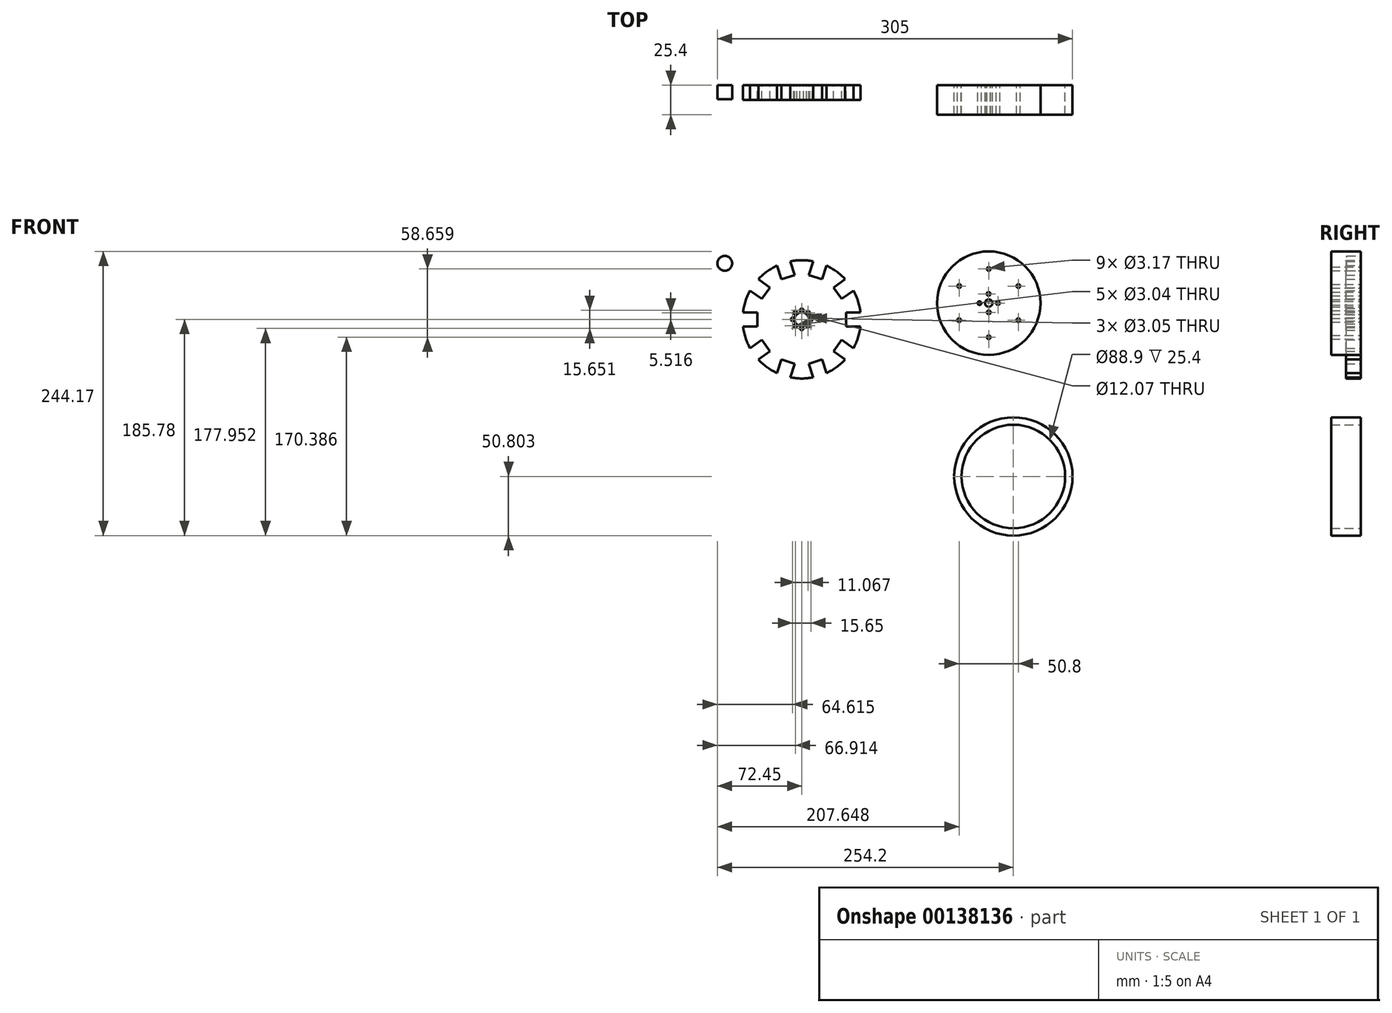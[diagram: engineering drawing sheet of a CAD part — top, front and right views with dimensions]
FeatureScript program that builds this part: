
annotation { "Feature Type Name" : "Feature", "Feature Type Description" : "" }
export const myFeature = defineFeature(function(context is Context, id is Id, definition is map)
    precondition{}
    {
        {
            var Q0;
            Q0=qCreatedBy(makeId("Front.planeOp"),FACE);
            var sketch = newSketch(context, id + "F0", { "sketchPlane" : qUnion([Q0])});
            skLineSegment(sketch, "E0.0", {"start": v(-6.03, 38.1) * mm, "end": v(6.03, 38.1) * mm});
            skLineSegment(sketch, "E0.2", {"start": v(17.51, 34.37) * mm, "end": v(27.28, 27.28) * mm});
            skLineSegment(sketch, "E0.4", {"start": v(34.37, 17.51) * mm, "end": v(38.1, 6.03) * mm});
            skLineSegment(sketch, "E0.6", {"start": v(38.1, -6.03) * mm, "end": v(34.37, -17.51) * mm});
            skLineSegment(sketch, "E0.8", {"start": v(27.28, -27.28) * mm, "end": v(17.51, -34.37) * mm});
            skLineSegment(sketch, "E0.10", {"start": v(6.03, -38.1) * mm, "end": v(-6.03, -38.1) * mm});
            skLineSegment(sketch, "E0.12", {"start": v(-17.51, -34.37) * mm, "end": v(-27.28, -27.28) * mm});
            skLineSegment(sketch, "E0.14", {"start": v(-34.37, -17.51) * mm, "end": v(-38.1, -6.03) * mm});
            skLineSegment(sketch, "E0.16", {"start": v(-38.1, 6.03) * mm, "end": v(-34.37, 17.51) * mm});
            skLineSegment(sketch, "E0.18", {"start": v(-27.28, 27.28) * mm, "end": v(-17.51, 34.37) * mm});
            skPoint(sketch, "E0.0.midPoint", {"position": v(0, 38.1) * mm});
            skLineSegment(sketch, "E1", {"start": v(6.03, 38.1) * mm, "end": v(9.85, 49.84) * mm});
            skLineSegment(sketch, "E2", {"start": v(-34.37, 17.51) * mm, "end": v(-44.35, 24.77) * mm});
            skLineSegment(sketch, "E3", {"start": v(-38.1, 6.03) * mm, "end": v(-50.44, 6.03) * mm});
            skLineSegment(sketch, "E4", {"start": v(-38.1, -6.03) * mm, "end": v(-50.44, -6.03) * mm});
            skLineSegment(sketch, "E5", {"start": v(-34.37, -17.51) * mm, "end": v(-44.35, -24.77) * mm});
            skLineSegment(sketch, "E6", {"start": v(-27.28, -27.28) * mm, "end": v(-37.26, -34.53) * mm});
            skLineSegment(sketch, "E7", {"start": v(-17.51, -34.37) * mm, "end": v(-21.33, -46.1) * mm});
            skLineSegment(sketch, "E8", {"start": v(-6.03, -38.1) * mm, "end": v(-9.85, -49.84) * mm});
            skLineSegment(sketch, "E9", {"start": v(6.03, -38.1) * mm, "end": v(9.85, -49.84) * mm});
            skLineSegment(sketch, "E10", {"start": v(17.51, -34.37) * mm, "end": v(21.33, -46.1) * mm});
            skLineSegment(sketch, "E11", {"start": v(27.28, -27.28) * mm, "end": v(37.26, -34.53) * mm});
            skLineSegment(sketch, "E12", {"start": v(34.37, -17.51) * mm, "end": v(44.35, -24.77) * mm});
            skLineSegment(sketch, "E13", {"start": v(38.1, -6.03) * mm, "end": v(50.44, -6.03) * mm});
            skLineSegment(sketch, "E14", {"start": v(38.1, 6.03) * mm, "end": v(50.44, 6.03) * mm});
            skLineSegment(sketch, "E15", {"start": v(34.37, 17.51) * mm, "end": v(44.35, 24.77) * mm});
            skLineSegment(sketch, "E16", {"start": v(27.28, 27.28) * mm, "end": v(37.26, 34.53) * mm});
            skLineSegment(sketch, "E17", {"start": v(17.51, 34.37) * mm, "end": v(21.33, 46.1) * mm});
            skArc(sketch, "E18", {"start": v(-21.33, 46.1) * mm, "mid": v(-29.86, 41.1) * mm, "end": v(-37.26, 34.53) * mm});
            skLineSegment(sketch, "E19", {"start": v(-27.28, 27.28) * mm, "end": v(-37.26, 34.53) * mm});
            skLineSegment(sketch, "E20", {"start": v(-17.51, 34.37) * mm, "end": v(-21.33, 46.1) * mm});
            skLineSegment(sketch, "E21", {"start": v(-9.85, 49.84) * mm, "end": v(-6.03, 38.1) * mm});
            skArc(sketch, "E22.trimOffspring", {"start": v(-44.35, 24.77) * mm, "mid": v(-48.31, 15.7) * mm, "end": v(-50.44, 6.03) * mm});
            skArc(sketch, "E23.trimOffspring", {"start": v(-50.44, -6.03) * mm, "mid": v(-48.31, -15.7) * mm, "end": v(-44.35, -24.77) * mm});
            skArc(sketch, "E24.trimOffspring", {"start": v(-9.85, -49.84) * mm, "mid": v(0, -50.8) * mm, "end": v(9.85, -49.84) * mm});
            skArc(sketch, "E25.trimOffspring", {"start": v(21.33, -46.1) * mm, "mid": v(29.86, -41.1) * mm, "end": v(37.26, -34.53) * mm});
            skArc(sketch, "E26.trimOffspring", {"start": v(-37.26, -34.53) * mm, "mid": v(-29.86, -41.1) * mm, "end": v(-21.33, -46.1) * mm});
            skArc(sketch, "E27.trimOffspring", {"start": v(9.85, 49.84) * mm, "mid": v(0, 50.8) * mm, "end": v(-9.85, 49.84) * mm});
            skArc(sketch, "E28.trimOffspring", {"start": v(37.26, 34.53) * mm, "mid": v(29.86, 41.1) * mm, "end": v(21.33, 46.1) * mm});
            skArc(sketch, "E29.trimOffspring", {"start": v(50.44, 6.03) * mm, "mid": v(48.31, 15.7) * mm, "end": v(44.35, 24.77) * mm});
            skArc(sketch, "E30.trimOffspring", {"start": v(44.35, -24.77) * mm, "mid": v(48.31, -15.7) * mm, "end": v(50.44, -6.03) * mm});
            skLineSegment(sketch, "E31", {"start": v(-38.1, -6.03) * mm, "end": v(-38.1, 6.03) * mm});
            skLineSegment(sketch, "E32", {"start": v(-34.37, 17.51) * mm, "end": v(-27.28, 27.28) * mm});
            skLineSegment(sketch, "E33", {"start": v(-17.51, 34.37) * mm, "end": v(-6.03, 38.1) * mm});
            skLineSegment(sketch, "E34", {"start": v(6.03, 38.1) * mm, "end": v(17.51, 34.37) * mm});
            skLineSegment(sketch, "E35", {"start": v(27.28, 27.28) * mm, "end": v(34.37, 17.51) * mm});
            skLineSegment(sketch, "E36", {"start": v(38.1, 6.03) * mm, "end": v(38.1, -6.03) * mm});
            skLineSegment(sketch, "E37", {"start": v(34.37, -17.51) * mm, "end": v(27.28, -27.28) * mm});
            skLineSegment(sketch, "E38", {"start": v(17.51, -34.37) * mm, "end": v(6.03, -38.1) * mm});
            skLineSegment(sketch, "E39", {"start": v(-6.03, -38.1) * mm, "end": v(-17.51, -34.37) * mm});
            skLineSegment(sketch, "E40", {"start": v(-27.28, -27.28) * mm, "end": v(-34.37, -17.51) * mm});
            skCircle(sketch, "E41", {"center": v(0, 0) * mm, "radius": 6.03 * mm});
            skCircle(sketch, "E42.cCircle", {"center": v(0, 0) * mm, "radius": 6.03 * mm, "construction": true});
            skPoint(sketch, "E42.0.midPoint", {"position": v(0, 6.03) * mm});
            skPoint(sketch, "E43.orphan", {"position": v(0, -6.03) * mm});
            skCircle(sketch, "E44", {"center": v(0, -7.83) * mm, "radius": 1.52 * mm});
            skPoint(sketch, "E45.orphan", {"position": v(0, -6.31) * mm});
            skPoint(sketch, "E46.start.orphan", {"position": v(0, -9.35) * mm});
            skPoint(sketch, "E47.orphan", {"position": v(4.27, -4.27) * mm});
            skPoint(sketch, "E48.orphan", {"position": v(2.5, -6.03) * mm});
            skCircle(sketch, "E49", {"center": v(5.53, -5.53) * mm, "radius": 1.52 * mm});
            skPoint(sketch, "E50.orphan", {"position": v(4.45, -4.45) * mm});
            skPoint(sketch, "E51.end.orphan", {"position": v(6.6, -6.6) * mm});
            skPoint(sketch, "E52.endSnap0", {"position": v(6.03, 0) * mm});
            skCircle(sketch, "E53", {"center": v(7.81, 0) * mm, "radius": 1.52 * mm});
            skPoint(sketch, "E54.orphan", {"position": v(9.34, 0) * mm});
            skPoint(sketch, "E52.start.orphan", {"position": v(6.3, 0) * mm});
            skPoint(sketch, "E42.2.end.orphan", {"position": v(6.03, -2.5) * mm});
            skPoint(sketch, "E55.orphan", {"position": v(4.27, 4.27) * mm});
            skCircle(sketch, "E56", {"center": v(5.53, 5.53) * mm, "radius": 1.52 * mm});
            skPoint(sketch, "E57.orphan", {"position": v(6.6, 6.6) * mm});
            skPoint(sketch, "E58.end.orphan", {"position": v(4.46, 4.46) * mm});
            skPoint(sketch, "E59.orphan", {"position": v(6.03, 2.5) * mm});
            skPoint(sketch, "E60.orphan", {"position": v(2.5, 6.03) * mm});
            skCircle(sketch, "E61", {"center": v(0, 7.82) * mm, "radius": 1.52 * mm});
            skPoint(sketch, "E62.orphan", {"position": v(0, 9.34) * mm});
            skPoint(sketch, "E63.start.orphan", {"position": v(0, 6.3) * mm});
            skPoint(sketch, "E64.orphan", {"position": v(-4.27, 4.27) * mm});
            skPoint(sketch, "E65.orphan", {"position": v(-2.5, 6.03) * mm});
            skCircle(sketch, "E66", {"center": v(-5.52, 5.52) * mm, "radius": 1.52 * mm});
            skPoint(sketch, "E67.orphan", {"position": v(-6.6, 6.6) * mm});
            skPoint(sketch, "E68.start.orphan", {"position": v(-4.44, 4.44) * mm});
            skPoint(sketch, "E69.endSnap0", {"position": v(-6.03, 0) * mm});
            skPoint(sketch, "E70.orphan", {"position": v(-6.03, 2.5) * mm});
            skCircle(sketch, "E71", {"center": v(-7.83, 0) * mm, "radius": 1.53 * mm});
            skPoint(sketch, "E72.orphan", {"position": v(-6.3, 0) * mm});
            skPoint(sketch, "E73.start.orphan", {"position": v(-9.36, 0) * mm});
            skPoint(sketch, "E74.orphan", {"position": v(-4.27, -4.27) * mm});
            skPoint(sketch, "E75.orphan", {"position": v(-2.5, -6.03) * mm});
            skPoint(sketch, "E42.5.end.orphan", {"position": v(-6.03, -2.5) * mm});
            skCircle(sketch, "E76", {"center": v(-5.54, -5.54) * mm, "radius": 1.52 * mm});
            skPoint(sketch, "E77.orphan", {"position": v(-4.46, -4.46) * mm});
            skPoint(sketch, "E78.end.orphan", {"position": v(-6.6, -6.6) * mm});
            skSolve(sketch);
        }
        {
            var Q0;
            Q0 = qSketchRegion(id + "F0", true);
            extrude(context, id + "F1", {"entities" : qUnion([Q0]), "depth" : 12.7 * mm});
        }
        {
            var Q0;
            Q0=qCreatedBy(makeId("Front.planeOp"),FACE);
            var sketch = newSketch(context, id + "F2", { "sketchPlane" : qUnion([Q0])});
            skCircle(sketch, "E79", {"center": v(-66.1, 48.1) * mm, "radius": 6.35 * mm});
            skSolve(sketch);
        }
        {
            var Q0;
            Q0 = qSketchRegion(id + "F2", true);
            extrude(context, id + "F3", {"entities" : qUnion([Q0]), "depth" : 12.06 * mm});
        }
        {
            var Q0;
            Q0=qCreatedBy(makeId("Front.planeOp"),FACE);
            var sketch = newSketch(context, id + "F4", { "sketchPlane" : qUnion([Q0])});
            skCircle(sketch, "E80", {"center": v(160.6, 13.94) * mm, "radius": 44.45 * mm});
            skCircle(sketch, "E81", {"center": v(160.6, 13.94) * mm, "radius": 3.18 * mm});
            skPoint(sketch, "E82.0.midPoint", {"position": v(186, 13.94) * mm});
            skCircle(sketch, "E83", {"center": v(135.2, 28.6) * mm, "radius": 1.59 * mm});
            skCircle(sketch, "E84", {"center": v(135.2, -0.73) * mm, "radius": 1.59 * mm});
            skCircle(sketch, "E85", {"center": v(160.6, -15.4) * mm, "radius": 1.59 * mm});
            skCircle(sketch, "E86", {"center": v(186, -0.73) * mm, "radius": 1.59 * mm});
            skCircle(sketch, "E87", {"center": v(186, 28.6) * mm, "radius": 1.59 * mm});
            skCircle(sketch, "E88", {"center": v(160.6, 43.27) * mm, "radius": 1.59 * mm});
            skPoint(sketch, "E89.orphan", {"position": v(160.39, 17.1) * mm});
            skCircle(sketch, "E90", {"center": v(160.39, 21.87) * mm, "radius": 1.59 * mm});
            skPoint(sketch, "E91.orphan", {"position": v(160.39, 20.28) * mm});
            skPoint(sketch, "E92.end.orphan", {"position": v(160.39, 23.45) * mm});
            skPoint(sketch, "E93.orphan", {"position": v(160.6, 10.76) * mm});
            skCircle(sketch, "E94", {"center": v(160.6, 6) * mm, "radius": 1.59 * mm});
            skPoint(sketch, "E95.orphan", {"position": v(160.6, 7.59) * mm});
            skPoint(sketch, "E96.start.orphan", {"position": v(160.6, 4.42) * mm});
            skPoint(sketch, "E97.orphan", {"position": v(163.77, 13.94) * mm});
            skCircle(sketch, "E98", {"center": v(168.53, 13.94) * mm, "radius": 1.59 * mm});
            skPoint(sketch, "E99.orphan", {"position": v(170.12, 13.94) * mm});
            skPoint(sketch, "E100.start.orphan", {"position": v(166.95, 13.94) * mm});
            skPoint(sketch, "E101.orphan", {"position": v(157.42, 13.94) * mm});
            skCircle(sketch, "E102", {"center": v(152.66, 13.94) * mm, "radius": 1.59 * mm});
            skPoint(sketch, "E103.orphan", {"position": v(154.25, 13.94) * mm});
            skPoint(sketch, "E104.end.orphan", {"position": v(151.07, 13.94) * mm});
            skSolve(sketch);
        }
        {
            var Q0;
            Q0 = qSketchRegion(id + "F4", true);
            extrude(context, id + "F5", {"entities" : qUnion([Q0]), "depth" : 25.4 * mm});
        }
        {
            var Q0;
            Q0=qCreatedBy(makeId("Front.planeOp"),FACE);
            var sketch = newSketch(context, id + "F6", { "sketchPlane" : qUnion([Q0])});
            skCircle(sketch, "E105", {"center": v(181.75, -134.98) * mm, "radius": 50.8 * mm});
            skCircle(sketch, "E106", {"center": v(181.75, -134.98) * mm, "radius": 44.45 * mm});
            skSolve(sketch);
        }
        {
            var Q0;
            Q0 = qSketchRegion(id + "F6", true);
            extrude(context, id + "F7", {"entities" : qUnion([Q0]), "depth" : 25.4 * mm});
        }
    });
